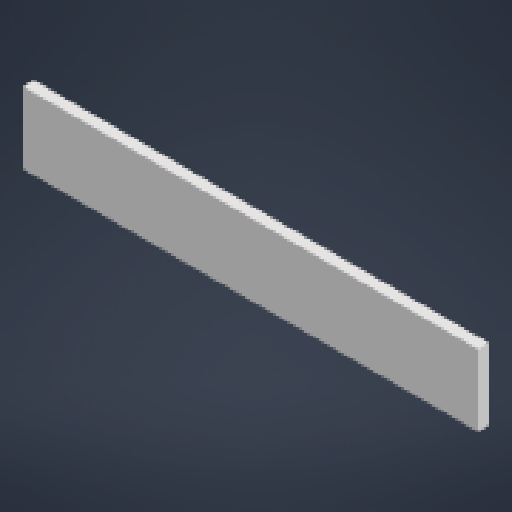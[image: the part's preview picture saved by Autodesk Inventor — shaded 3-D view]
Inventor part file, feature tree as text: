
AUTODESK INVENTOR PART (.ipt)
format: ipt  version: 2024 (Build 280153000, 153)  size: 276,992 bytes
history: native  units: mm
features: extrude x7, sketch x6, other x4, projected_geometry x3, reference x2
ambient origin geometry x8: Origin, YZ Plane, XZ Plane, XY Plane, X Axis, Y Axis, Z Axis, Center Point
bodies: Body1 (feature_tree)
feature tree (22):
  other  "솔리드1"
  extrude  "돌출1"  Depth=5.0mm TaperAngle=0.0deg
  extrude  "돌출2"  Depth=128.0mm
  extrude  "돌출3"  Depth=32.0mm
  extrude  "돌출4"  Depth=207.0mm
  sketch  "스케치5"
  extrude  "돌출5"  Depth=103.5mm
  extrude  "돌출6"  Depth=32.526912mm
  extrude  "돌출7"  Depth=5.0mm TaperAngle=0.0deg
  sketch  "스케치1"
  reference  "참조1"
  reference  "참조2"
  sketch  "스케치2"
  projected_geometry  "투영된 루프1"
  sketch  "스케치3"
  sketch  "스케치4"
  projected_geometry  "투영된 루프2"
  sketch  "스케치7"
  projected_geometry  "투영된 루프3"
  other  "<userpath>\Downloads\AAST\PART\AAST Remote Controler\AASTRC case.iam"
  other  "AASTRC case.iam"
  other  "AASTRC Bottom case:1"
